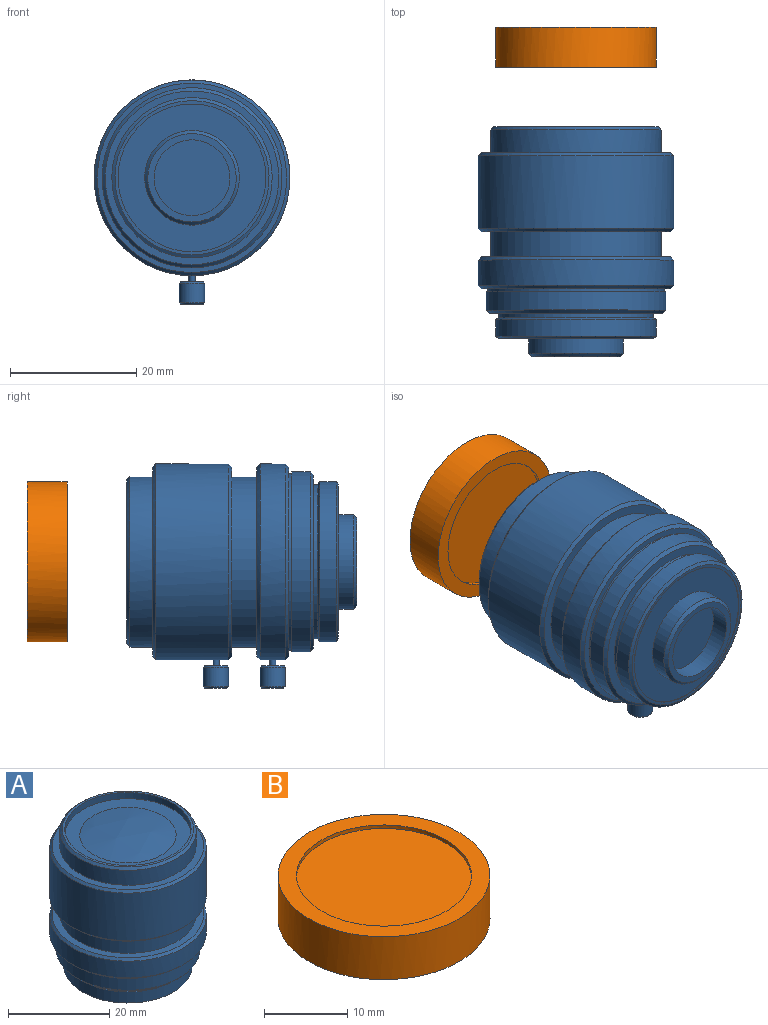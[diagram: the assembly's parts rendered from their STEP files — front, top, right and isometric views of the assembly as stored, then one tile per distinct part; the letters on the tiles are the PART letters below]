
ASSEMBLY  parts=2 mates=1
PART A: 46 faces, bbox 31x35.5x36.4 mm
  f0: cylinder r=0.5mm len=1mm, axis (0,-1,0), area 3.1mm2, adj f29,f45
  f1: cone r=1.79mm half-angle=45deg, axis (0,1,0), area 3.6mm2, adj f2,f45
  f2: cylinder r=2mm len=4mm, axis (0,-1,0), area 38.2mm2, adj f1,f3
  f3: cone r=2mm half-angle=45deg, axis (0,-1,0), area 4.2mm2, adj f2,f44
  f4: cylinder r=0.5mm len=1.01mm, axis (0,-1,0), area 3.2mm2, adj f28,f43
  f5: cone r=1.79mm half-angle=45deg, axis (0,1,0), area 3.6mm2, adj f6,f43
  f6: cylinder r=2mm len=4mm, axis (0,-1,0), area 38.2mm2, adj f5,f7
  f7: cone r=2mm half-angle=45deg, axis (0,-1,0), area 4.2mm2, adj f6,f42
  f8: cone r=15.5mm half-angle=45deg, axis (0,0,-1), area 67.8mm2, adj f28,f30
  f9: cone r=15mm half-angle=45deg, axis (0,0,1), area 67.8mm2, adj f28,f31
  f10: cone r=15.5mm half-angle=45deg, axis (0,0,-1), area 67.8mm2, adj f29,f32
  f11: cone r=15mm half-angle=45deg, axis (0,0,1), area 67.8mm2, adj f29,f33
  f12: cone r=13.75mm half-angle=45deg, axis (0,0,1), area 62.2mm2, adj f25,f35
  f13: cone r=7mm half-angle=45deg, axis (0,0,1), area 32.2mm2, adj f19,f38
  f14: cone r=13.5mm half-angle=45deg, axis (0,0,-1), area 58.9mm2, adj f15,f41
  f15: cylinder r=13.5mm len=27mm, axis (0,0,-1), area 305.4mm2, adj f14,f30
  f16: cylinder r=12.5mm len=25mm, axis (0,0,-1), area 117.8mm2, adj f40,f41
  f17: sphere r=46mm, area 289mm2, adj f40
  f18: cylinder r=6mm len=12mm, axis (0,0,-1), area 109.3mm2, adj f38,f39
  f19: cylinder r=7.5mm len=15mm, axis (0,0,-1), area 117.8mm2, adj f13,f37
  f20: cylinder r=11.7mm len=23.4mm, axis (0,0,-1), area 7.4mm2, adj f36,f37
  f21: cone r=12.2mm half-angle=59.5deg, axis (0,0,1), area 45.4mm2, adj f22,f36
  f22: cylinder r=12.7mm len=25.4mm, axis (0,0,-1), area 214.7mm2, adj f21,f23
  f23: cone r=12.7mm half-angle=59.5deg, axis (0,0,-1), area 45.4mm2, adj f22,f24
  f24: cylinder r=12.2mm len=24.4mm, axis (0,0,-1), area 53.3mm2, adj f23,f35
  f25: cylinder r=14.25mm len=28.5mm, axis (0,0,-1), area 259.7mm2, adj f12,f34
  f26: cylinder r=14mm len=28mm, axis (0,0,-1), area 44mm2, adj f33,f34
  f27: cylinder r=13.5mm len=27mm, axis (0,0,-1), area 339.3mm2, adj f31,f32
  f28: cylinder r=15.5mm len=31mm, axis (0,0,-1), area 1119.3mm2, adj f4,f8,f9
  f29: cylinder r=15.5mm len=31mm, axis (0,0,-1), area 391.6mm2, adj f0,f10,f11
  f30: plane 30x30mm, normal (0,0,1), area 134.3mm2, adj f8,f15
  f31: plane 30x30mm, normal (0,0,-1), area 134.3mm2, adj f9,f27
  f32: plane 30x30mm, normal (0,0,1), area 134.3mm2, adj f10,f27
  f33: plane 30x30mm, normal (0,0,-1), area 91.1mm2, adj f11,f26
  f34: plane 28.5x28.5mm, normal (0,0,1), area 22.2mm2, adj f25,f26
  f35: plane 27.5x27.5mm, normal (0,0,-1), area 126.4mm2, adj f12,f24
  f36: plane 24.4x24.4mm, normal (0,0,-1), area 37.5mm2, adj f20,f21
  f37: plane 23.4x23.4mm, normal (0,0,-1), area 253.3mm2, adj f19,f20
  f38: plane 14x14mm, normal (0,0,-1), area 40.8mm2, adj f13,f18
  f39: plane 12x12mm, normal (0,0,-1), area 113.1mm2, adj f18
  f40: plane 25x25mm, normal (0,0,1), area 205mm2, adj f16,f17
  f41: plane 26x26mm, normal (0,0,1), area 40.1mm2, adj f14,f16
  f42: plane 3.5x3.5mm, normal (0,1,0), area 9.6mm2, adj f7
  f43: plane 3.57x3.57mm, normal (0,-1,0), area 9.2mm2, adj f4,f5
  f44: plane 3.5x3.5mm, normal (0,1,0), area 9.6mm2, adj f3
  f45: plane 3.57x3.57mm, normal (0,-1,0), area 9.2mm2, adj f0,f1
PART B: 7 faces, bbox 25.4x25.4x6.3 mm
  f0: plane 21x21mm, normal (0,0,1), area 346.4mm2, adj f1
  f1: cylinder r=10.5mm len=21mm, axis (0,0,1), area 33.5mm2, adj f0,f2
  f2: plane 25.4x25.4mm, normal (0,0,1), area 160.3mm2, adj f1,f3
  f3: cylinder r=12.7mm len=25.4mm, axis (0,0,-1), area 502.7mm2, adj f2,f4
  f4: plane 25.4x25.4mm, normal (0,0,-1), area 160.3mm2, adj f3,f6
  f5: plane 21x21mm, normal (0,0,-1), area 346.4mm2, adj f6
  f6: cylinder r=10.5mm len=21mm, axis (0,0,-1), area 33.5mm2, adj f4,f5
PLACE A rot(axis=(-1,0,0),90deg) t=(0,15.3,0)mm
PLACE B rot(axis=(-1,0,0),90deg) t=(-4.51,36.65,1.58)mm
MATE slider B.f1 <-> A.f13  axis (0,-1,0) through (0,43.46,0)mm
